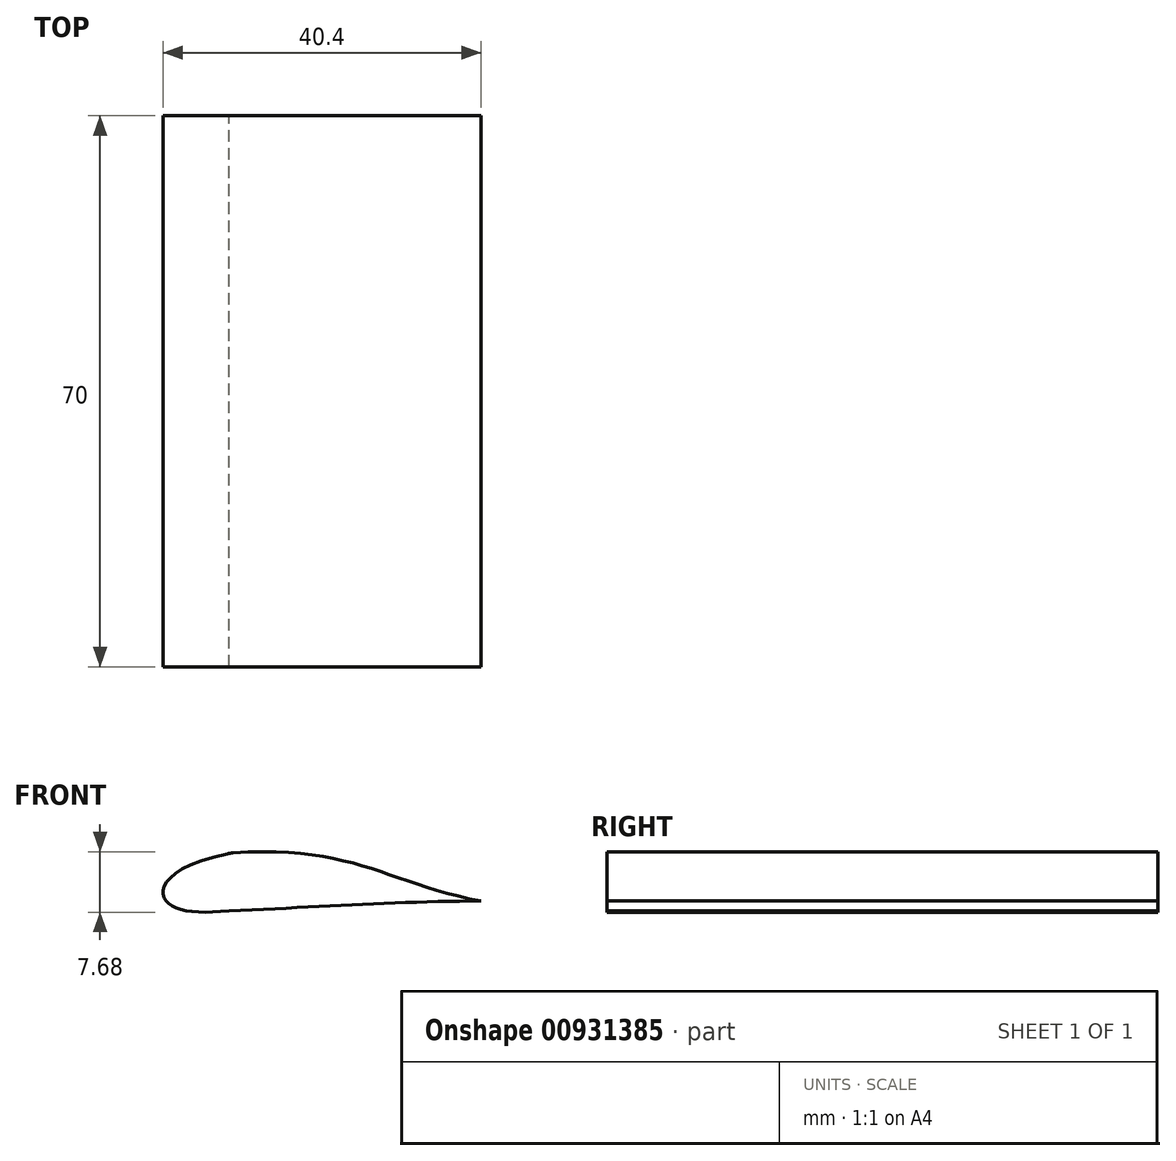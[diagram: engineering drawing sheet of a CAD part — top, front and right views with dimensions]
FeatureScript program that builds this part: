
annotation { "Feature Type Name" : "Feature", "Feature Type Description" : "" }
export const myFeature = defineFeature(function(context is Context, id is Id, definition is map)
    precondition{}
    {
        {
            var Q0;
            Q0=qCreatedBy(makeId("Front.planeOp"),FACE);
            var sketch = newSketch(context, id + "F0", { "sketchPlane" : qUnion([Q0])});
            skFitSpline(sketch, "E0", {"points": [v(8.15, 6.1) * mm, v(0, 0) * mm, v(7.98, -1.24) * mm], "startDerivative": vector(-46.23, -9.42) * mm, "endDerivative": vector(24.88, 2.58) * mm});
            skFitSpline(sketch, "E1", {"points": [v(8.15, 6.1) * mm, v(40, 0) * mm], "startDerivative": vector(46.61, 3.5) * mm, "endDerivative": vector(35.97, -6.82) * mm});
            skFitSpline(sketch, "E2", {"points": [v(40, 0) * mm, v(7.98, -1.24) * mm], "startDerivative": vector(-31.8, 0) * mm, "endDerivative": vector(-34.22, -1.45) * mm});
            skArc(sketch, "E3.filletArc", {"start": v(8.92, 6.13) * mm, "mid": v(8.36, 6.1) * mm, "end": v(7.8, 6.02) * mm});
            skArc(sketch, "E4.filletArc", {"start": v(8.5, 6.12) * mm, "mid": v(8.15, 6.08) * mm, "end": v(7.8, 6.02) * mm});
            skSolve(sketch);
        }
        {
            var Q0;
            Q0=makeQuery(id+"F0.imprint","IMPRINT",FACE,{"disambiguationData":[TD([[makeQuery(id+"F0.imprint","IMPRINT",EDGE,{"derivedFrom":sQuery(id+"F0.wireOp",EDGE,"E0")}),1.0]])]});
            extrude(context, id + "F1", {"entities" : qUnion([Q0]), "depth" : 70 * mm, "offsetDistance" : 25 * mm});
        }
        {
            var Q0;
            Q0=qCreatedBy(makeId("Front.planeOp"),FACE);
            cPlane(context, id + "F2", {"entities" : qUnion([Q0]), "cplaneType" : CPlaneType.OFFSET, "offset" : 100 * mm, "width" : 150 * mm, "height" : 150 * mm});
        }
    });
